# Revit family: HGPR48_Revit
name_source: partatom
category: Specialty Equipment
revit_build: Autodesk Revit MEP 2014 (Build: 20130308_1515(x64)
units: mm (PartAtom-declared; Revit-internal decimal feet)

## types (1)
- HGPR48
    Adjustment = Stainless Steel
    BAKING STONE = ABS16
    BRASS/BLACK PORCELAIN BURNER CAPS = 6/EA
    BROIL/ROASTING PAN W/GRILL & V RACK = AORPVR
    Burner = Plastic-Black
    CAVITY = BLACK ENAMEL COATING
    CENTER FRONT (BTU) = 15,000 STACK DUAL (SIMMER)
    CENTER REAR (BTU) = 15,000 STACK DUAL (SIMMER)
    CIRCUIT BREAKER (A) = 15 AMPS
    CLEANING TYPE = SELF-CLEAN (BOTH)
    COOKIE SHEETS (SET OF 3) = ACSRO303
    COOKING MODES = CONVECTION BAKE; BAKE CONVECTION BROIL; BROIL
    Depth = 24"
    Description = 48-INCH PRO DUAL-FUEL RANGE HERIT AGE COLLECTION
    Door = Stainless Steel
    ENERGY SOURCE = GAS AND ELECTRICAL
    FREQUENCY (HZ) = 60 HZ
    GAS TYPES = NATURAL GAS, NATURAL GAS (HIGH ALTITUDE), LIQUID PROPANE LIQUID PROPANE (HIGH ALTITUDE)
    GLIDERACK™ = 2 (LG) & 2 (SM)
    Gas Burner = Stainless Steel
    Glide = Plastic-Black
    HIDDEN STAINLESS STEEL BAKE BURNER = 24,000 BTU (LG) 15,000 BTU (SM)
    HIGHLIGHTING COLOR = WHITE
    Handle = Stainless Steel
    Height = 37 1/2"
    ILLUMINA™ BURNER KNOBS = YES
    INFRARED CERAMIC BROIL GAS BURNER = 18,000 BTU (LG) 13,000 BTU (SM)
    KEEP WARM = YES (BOTH)
    LED (WHITE) = YES
    LEFT FRONT (BTU) = 18,000 DUAL (SIMMER/SEAR)
    LEFT REAR (BTU) = 15,000 STACK DUAL (SIMMER)
    LIGHTING = LED & HALOGEN
    LIMITED, PARTS AND LABOR = 1 YEAR
    Manufacturer = Dacor
    Model = HGPR48
    NUMBER OF KNOBS = 7 KNOBS
    OVEN CAPACITY (CUBIC FEET) = 5.2 (LG OVEN) / 2.8 (SM OVEN)
    OVEN CONTROL METHOD = KNOBS
    OVEN RACK POSITIONS = 6 (LG) / 6 (SM)
    PERMA-FLAME™ (AUTO RE-IGNITION) = YES
    PLUG TYPE = GROUNDED, DEDICATED,3-PRONG ELECTRICAL OUTLET
    REMOVABLE CONVECTION FILTER = 1/EA OVEN
    REMOVABLE NON-STICK GRIDDLE = 1
    REMOVABLE NON-STICK SEARING GRILL = AEGR36
    RIGHT FRONT (BTU) = 18,000 STACK DUAL (SIMMER/SEAR)
    RIGHT REAR (BTU) = 15,000 STACK DUAL (SIMMER)
    SEALED BURNERS = YES
    STAINLESS STEEL BACKGUARD 1 1/2” = APB30GLP
    STAINLESS STEEL BACKGUARD 9” = APB30G9
    STANDARD RACK = 1 (LG) / 1 (SM)
    Support = Glass
    TEMPERATURE (F/C) = YES
    TOTAL NUMBER OF COOKTOP BURNERS = 6 DUAL STACK BRASS BURNERS
    TYPE OF GRATE = CONTINUOUS CAST IRON
    Unit = Stainless Steel
    VOLTS (V) = 120 VAC
    WOK RING = 1
    Width = 48"

## geometry (parser evidence)
native form markers: Blend x4, Sweep x3
no freeform markers — native parametric forms only
